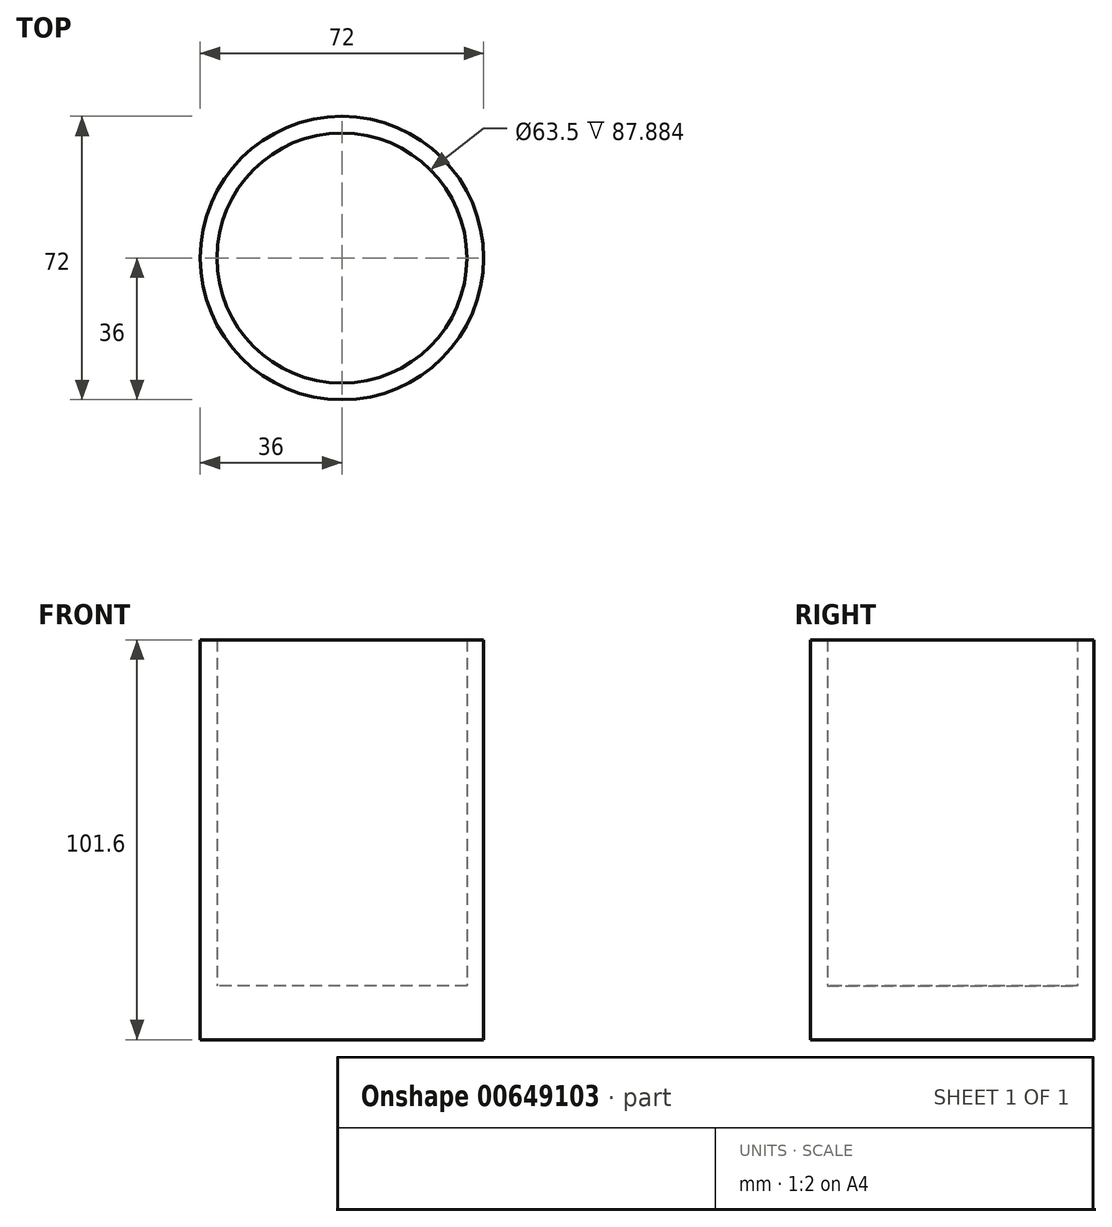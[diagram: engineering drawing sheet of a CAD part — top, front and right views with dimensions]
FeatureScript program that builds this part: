
annotation { "Feature Type Name" : "Feature", "Feature Type Description" : "" }
export const myFeature = defineFeature(function(context is Context, id is Id, definition is map)
    precondition{}
    {
        {
            var Q0;
            Q0=qCreatedBy(makeId("Top.planeOp"),FACE);
            var sketch = newSketch(context, id + "F0", { "sketchPlane" : qUnion([Q0])});
            skCircle(sketch, "E0", {"center": v(0, 0) * mm, "radius": 31.75 * mm});
            skCircle(sketch, "E1", {"center": v(0, 0) * mm, "radius": 36 * mm});
            skSolve(sketch);
        }
        {
            var Q0;
            Q0 = qSketchRegion(id + "F0", true);
            extrude(context, id + "F1", {"entities" : qUnion([Q0]), "depth" : 101.6 * mm, "offsetDistance" : 25.4 * mm});
        }
        {
            var Q0;
            Q0=makeQuery(id+"F1.opExtrude","CAP_FACE",FACE,{"disambiguationData":[OSD([sQuery(id+"F0.wireOp",EDGE,"E0"),sQuery(id+"F0.wireOp",EDGE,"E1")])],"isStart":true});
            var sketch = newSketch(context, id + "F2", { "sketchPlane" : qUnion([Q0])});
            skCircle(sketch, "E2", {"center": v(0, 0) * mm, "radius": 32.31 * mm});
            skSolve(sketch);
        }
        {
            var Q0;
            Q0=makeQuery(id+"F2.imprint","IMPRINT",FACE,{"disambiguationData":[TD([[makeQuery(id+"F2.imprint","IMPRINT",EDGE,{"derivedFrom":sQuery(id+"F2.wireOp",EDGE,"E2")}),-1.0]])]});
            var Q1;
            Q1=makeQuery(id+"F2.imprint","IMPRINT",FACE,{"disambiguationData":[TD([[makeQuery(id+"F2.imprint","IMPRINT",EDGE,{"derivedFrom":makeQuery(id+"F1.opExtrude","CAP_EDGE",EDGE,{"disambiguationData":[OSD([sQuery(id+"F0.wireOp",EDGE,"E0")])],"isStart":true})}),-1.0]])]});
            extrude(context, id + "F3", {"entities" : qUnion([Q0, Q1]), "operationType" : NewBodyOperationType.ADD, "oppositeDirection" : true, "depth" : 13.72 * mm, "offsetDistance" : 25.4 * mm});
        }
        {
            var Q0;
            Q0=qCreatedBy(makeId("Right.planeOp"),FACE);
            cPlane(context, id + "F4", {"entities" : qUnion([Q0]), "cplaneType" : CPlaneType.OFFSET, "offset" : 34.04 * mm, "width" : 152.4 * mm, "height" : 152.4 * mm});
        }
    });
